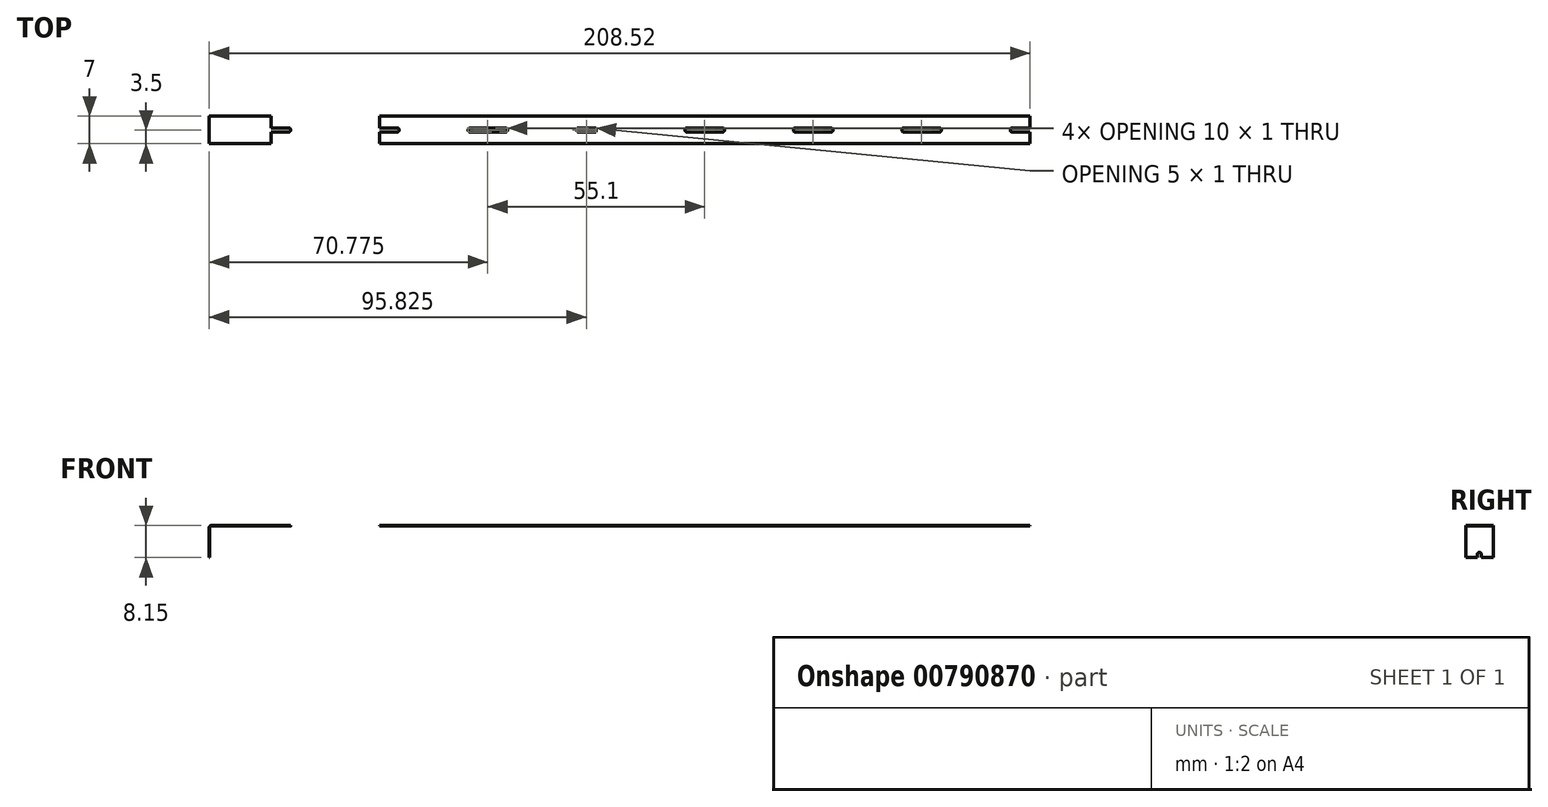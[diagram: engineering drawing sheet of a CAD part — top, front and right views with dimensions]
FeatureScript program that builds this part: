
annotation { "Feature Type Name" : "Feature", "Feature Type Description" : "" }
export const myFeature = defineFeature(function(context is Context, id is Id, definition is map)
    precondition{}
    {
        {
            var Q0;
            Q0=qCreatedBy(makeId("Top.planeOp"),FACE);
            var sketch = newSketch(context, id + "F0", { "sketchPlane" : qUnion([Q0])});
            skPoint(sketch, "E0.middle", {"position": v(0, 0) * mm});
            skLineSegment(sketch, "E1.bottom", {"start": v(-9.18, -0.5) * mm, "end": v(-13.77, -0.5) * mm});
            skLineSegment(sketch, "E1.top", {"start": v(-9.18, 0.5) * mm, "end": v(-13.77, 0.5) * mm});
            skLineSegment(sketch, "E1.left", {"start": v(-8.78, -0.1) * mm, "end": v(-8.78, 0.1) * mm});
            skLineSegment(sketch, "E1.right", {"start": v(-18.78, -0.1) * mm, "end": v(-18.78, 0.1) * mm});
            skPoint(sketch, "E1.middle", {"position": v(-13.78, 0) * mm});
            skPoint(sketch, "E2.visualSharp", {"position": v(-8.78, 0.5) * mm});
            skArc(sketch, "E2.filletArc", {"start": v(-8.78, 0.1) * mm, "mid": v(-8.9, 0.38) * mm, "end": v(-9.18, 0.5) * mm});
            skPoint(sketch, "E3.visualSharp", {"position": v(-8.78, -0.5) * mm});
            skArc(sketch, "E3.filletArc", {"start": v(-9.18, -0.5) * mm, "mid": v(-8.9, -0.38) * mm, "end": v(-8.78, -0.1) * mm});
            skPoint(sketch, "E4.visualSharp", {"position": v(-18.78, 0.5) * mm});
            skArc(sketch, "E4.filletArc", {"start": v(-18.38, 0.5) * mm, "mid": v(-18.66, 0.38) * mm, "end": v(-18.77, 0.1) * mm});
            skPoint(sketch, "E5.visualSharp", {"position": v(-18.78, -0.5) * mm});
            skArc(sketch, "E5.filletArc", {"start": v(-18.77, -0.1) * mm, "mid": v(-18.66, -0.38) * mm, "end": v(-18.38, -0.5) * mm});
            skLineSegment(sketch, "E6", {"start": v(0, 3.5) * mm, "end": v(-13.78, 3.5) * mm});
            skPoint(sketch, "E6.endSnap0", {"position": v(-13.77, 0.5) * mm});
            skLineSegment(sketch, "E7", {"start": v(-13.78, 3.5) * mm, "end": v(-13.78, 0.5) * mm});
            skLineSegment(sketch, "E8.MirrorCS", {"start": v(0, -3.5) * mm, "end": v(-13.78, -3.5) * mm});
            skLineSegment(sketch, "E9.MirrorCS", {"start": v(-13.78, -3.5) * mm, "end": v(-13.78, -0.5) * mm});
            skLineSegment(sketch, "E10.MirrorCS", {"start": v(0, 3.5) * mm, "end": v(13.78, 3.5) * mm});
            skLineSegment(sketch, "E11.MirrorCS", {"start": v(0, -3.5) * mm, "end": v(13.78, -3.5) * mm});
            skLineSegment(sketch, "E12.MirrorCS", {"start": v(8.78, -0.1) * mm, "end": v(8.78, 0.1) * mm});
            skArc(sketch, "E13.MirrorCS", {"start": v(8.78, 0.1) * mm, "mid": v(8.9, 0.38) * mm, "end": v(9.18, 0.5) * mm});
            skArc(sketch, "E14.MirrorCS", {"start": v(18.77, -0.1) * mm, "mid": v(18.66, -0.38) * mm, "end": v(18.38, -0.5) * mm});
            skLineSegment(sketch, "E15.MirrorCS", {"start": v(18.78, -0.1) * mm, "end": v(18.78, 0.1) * mm});
            skArc(sketch, "E16.MirrorCS", {"start": v(18.38, 0.5) * mm, "mid": v(18.66, 0.38) * mm, "end": v(18.77, 0.1) * mm});
            skArc(sketch, "E17.MirrorCS", {"start": v(9.18, -0.5) * mm, "mid": v(8.9, -0.38) * mm, "end": v(8.78, -0.1) * mm});
            skPoint(sketch, "E18.MirrorP", {"position": v(18.78, 0.5) * mm});
            skLineSegment(sketch, "E19.MirrorCS", {"start": v(9.18, 0.5) * mm, "end": v(18.38, 0.5) * mm});
            skLineSegment(sketch, "E20.MirrorCS", {"start": v(9.18, -0.5) * mm, "end": v(18.38, -0.5) * mm});
            skPoint(sketch, "E21.MirrorP", {"position": v(13.77, 0.5) * mm});
            skPoint(sketch, "E22.MirrorP", {"position": v(8.78, 0.5) * mm});
            skPoint(sketch, "E23.MirrorP", {"position": v(18.78, -0.5) * mm});
            skPoint(sketch, "E24.MirrorP", {"position": v(8.78, -0.5) * mm});
            skPoint(sketch, "E25.MirrorP", {"position": v(13.78, 0) * mm});
            skLineSegment(sketch, "E26.MirrorCS", {"start": v(13.78, 3.5) * mm, "end": v(13.78, 0.5) * mm});
            skLineSegment(sketch, "E27.MirrorCS", {"start": v(13.78, -3.5) * mm, "end": v(13.78, -0.5) * mm});
            skPoint(sketch, "E28.1.0.0", {"position": v(36.33, 0.5) * mm});
            skLineSegment(sketch, "E28.1.0.1", {"start": v(27.55, 3.5) * mm, "end": v(41.33, 3.5) * mm});
            skLineSegment(sketch, "E28.1.0.2", {"start": v(36.73, -0.5) * mm, "end": v(45.93, -0.5) * mm});
            skPoint(sketch, "E28.1.0.3", {"position": v(27.55, 0) * mm});
            skLineSegment(sketch, "E28.1.0.4", {"start": v(27.55, -3.5) * mm, "end": v(41.33, -3.5) * mm});
            skPoint(sketch, "E28.1.0.5", {"position": v(41.33, 0.5) * mm});
            skPoint(sketch, "E28.1.0.6", {"position": v(41.33, 0) * mm});
            skPoint(sketch, "E28.1.0.7", {"position": v(46.33, -0.5) * mm});
            skPoint(sketch, "E28.1.0.8", {"position": v(36.33, -0.5) * mm});
            skLineSegment(sketch, "E28.1.0.9", {"start": v(27.55, -3.5) * mm, "end": v(13.78, -3.5) * mm});
            skLineSegment(sketch, "E28.1.0.10", {"start": v(36.73, 0.5) * mm, "end": v(45.93, 0.5) * mm});
            skLineSegment(sketch, "E28.1.0.11", {"start": v(27.55, 3.5) * mm, "end": v(13.78, 3.5) * mm});
            skLineSegment(sketch, "E28.1.0.12", {"start": v(41.33, 3.5) * mm, "end": v(41.33, 0.5) * mm});
            skLineSegment(sketch, "E28.1.0.13", {"start": v(41.33, -3.5) * mm, "end": v(41.33, -0.5) * mm});
            skPoint(sketch, "E28.1.0.14", {"position": v(46.33, 0.5) * mm});
            skArc(sketch, "E28.1.0.15", {"start": v(45.93, 0.5) * mm, "mid": v(46.2, 0.38) * mm, "end": v(46.32, 0.1) * mm});
            skArc(sketch, "E28.1.0.16", {"start": v(36.73, -0.5) * mm, "mid": v(36.44, -0.38) * mm, "end": v(36.33, -0.1) * mm});
            skArc(sketch, "E28.1.0.17", {"start": v(46.33, -0.1) * mm, "mid": v(46.2, -0.38) * mm, "end": v(45.93, -0.5) * mm});
            skArc(sketch, "E28.1.0.18", {"start": v(36.33, 0.1) * mm, "mid": v(36.44, 0.38) * mm, "end": v(36.73, 0.5) * mm});
            skLineSegment(sketch, "E28.1.0.19", {"start": v(36.32, -0.1) * mm, "end": v(36.32, 0.1) * mm});
            skLineSegment(sketch, "E28.1.0.20", {"start": v(46.33, -0.1) * mm, "end": v(46.33, 0.1) * mm});
            skPoint(sketch, "E28.2.0.0", {"position": v(63.88, 0.5) * mm});
            skLineSegment(sketch, "E28.2.0.1", {"start": v(55.1, 3.5) * mm, "end": v(68.88, 3.5) * mm});
            skLineSegment(sketch, "E28.2.0.2", {"start": v(64.28, -0.5) * mm, "end": v(73.48, -0.5) * mm});
            skPoint(sketch, "E28.2.0.3", {"position": v(55.1, 0) * mm});
            skLineSegment(sketch, "E28.2.0.4", {"start": v(55.1, -3.5) * mm, "end": v(68.88, -3.5) * mm});
            skPoint(sketch, "E28.2.0.5", {"position": v(68.88, 0.5) * mm});
            skPoint(sketch, "E28.2.0.6", {"position": v(68.88, 0) * mm});
            skPoint(sketch, "E28.2.0.7", {"position": v(73.88, -0.5) * mm});
            skPoint(sketch, "E28.2.0.8", {"position": v(63.88, -0.5) * mm});
            skLineSegment(sketch, "E28.2.0.9", {"start": v(55.1, -3.5) * mm, "end": v(41.33, -3.5) * mm});
            skLineSegment(sketch, "E28.2.0.10", {"start": v(64.28, 0.5) * mm, "end": v(73.48, 0.5) * mm});
            skLineSegment(sketch, "E28.2.0.11", {"start": v(55.1, 3.5) * mm, "end": v(41.33, 3.5) * mm});
            skLineSegment(sketch, "E28.2.0.12", {"start": v(68.88, 3.5) * mm, "end": v(68.88, 0.5) * mm});
            skLineSegment(sketch, "E28.2.0.13", {"start": v(68.88, -3.5) * mm, "end": v(68.88, -0.5) * mm});
            skPoint(sketch, "E28.2.0.14", {"position": v(73.88, 0.5) * mm});
            skArc(sketch, "E28.2.0.15", {"start": v(73.48, 0.5) * mm, "mid": v(73.76, 0.38) * mm, "end": v(73.88, 0.1) * mm});
            skArc(sketch, "E28.2.0.16", {"start": v(64.28, -0.5) * mm, "mid": v(64, -0.38) * mm, "end": v(63.88, -0.1) * mm});
            skArc(sketch, "E28.2.0.17", {"start": v(73.88, -0.1) * mm, "mid": v(73.76, -0.38) * mm, "end": v(73.48, -0.5) * mm});
            skArc(sketch, "E28.2.0.18", {"start": v(63.88, 0.1) * mm, "mid": v(64, 0.38) * mm, "end": v(64.28, 0.5) * mm});
            skLineSegment(sketch, "E28.2.0.19", {"start": v(63.88, -0.1) * mm, "end": v(63.88, 0.1) * mm});
            skLineSegment(sketch, "E28.2.0.20", {"start": v(73.88, -0.1) * mm, "end": v(73.88, 0.1) * mm});
            skPoint(sketch, "E28.3.0.0", {"position": v(91.43, 0.5) * mm});
            skLineSegment(sketch, "E28.3.0.1", {"start": v(82.65, 3.5) * mm, "end": v(96.43, 3.5) * mm});
            skLineSegment(sketch, "E28.3.0.2", {"start": v(91.83, -0.5) * mm, "end": v(101.03, -0.5) * mm});
            skPoint(sketch, "E28.3.0.3", {"position": v(82.65, 0) * mm});
            skLineSegment(sketch, "E28.3.0.4", {"start": v(82.65, -3.5) * mm, "end": v(96.43, -3.5) * mm});
            skPoint(sketch, "E28.3.0.5", {"position": v(96.43, 0.5) * mm});
            skPoint(sketch, "E28.3.0.6", {"position": v(96.42, 0) * mm});
            skPoint(sketch, "E28.3.0.7", {"position": v(101.42, -0.5) * mm});
            skPoint(sketch, "E28.3.0.8", {"position": v(91.43, -0.5) * mm});
            skLineSegment(sketch, "E28.3.0.9", {"start": v(82.65, -3.5) * mm, "end": v(68.88, -3.5) * mm});
            skLineSegment(sketch, "E28.3.0.10", {"start": v(91.83, 0.5) * mm, "end": v(101.03, 0.5) * mm});
            skLineSegment(sketch, "E28.3.0.11", {"start": v(82.65, 3.5) * mm, "end": v(68.88, 3.5) * mm});
            skLineSegment(sketch, "E28.3.0.12", {"start": v(96.43, 3.5) * mm, "end": v(96.43, 0.5) * mm});
            skLineSegment(sketch, "E28.3.0.13", {"start": v(96.43, -3.5) * mm, "end": v(96.43, -0.5) * mm});
            skPoint(sketch, "E28.3.0.14", {"position": v(101.42, 0.5) * mm});
            skArc(sketch, "E28.3.0.15", {"start": v(101.03, 0.5) * mm, "mid": v(101.3, 0.38) * mm, "end": v(101.42, 0.1) * mm});
            skArc(sketch, "E28.3.0.16", {"start": v(91.83, -0.5) * mm, "mid": v(91.54, -0.38) * mm, "end": v(91.43, -0.1) * mm});
            skArc(sketch, "E28.3.0.17", {"start": v(101.42, -0.1) * mm, "mid": v(101.3, -0.38) * mm, "end": v(101.03, -0.5) * mm});
            skArc(sketch, "E28.3.0.18", {"start": v(91.43, 0.1) * mm, "mid": v(91.54, 0.38) * mm, "end": v(91.83, 0.5) * mm});
            skLineSegment(sketch, "E28.3.0.19", {"start": v(91.43, -0.1) * mm, "end": v(91.43, 0.1) * mm});
            skLineSegment(sketch, "E28.3.0.20", {"start": v(101.42, -0.1) * mm, "end": v(101.42, 0.1) * mm});
            skLineSegment(sketch, "E28.direction1", {"start": v(-13.78, -3.5) * mm, "end": v(13.78, -3.5) * mm, "construction": true});
            skLineSegment(sketch, "E29", {"start": v(0, 3.5) * mm, "end": v(0, -3.5) * mm});
            skLineSegment(sketch, "E30.bottom", {"start": v(96.43, -3.5) * mm, "end": v(99.43, -3.5) * mm});
            skLineSegment(sketch, "E30.top", {"start": v(96.43, 3.5) * mm, "end": v(99.43, 3.5) * mm});
            skLineSegment(sketch, "E30.left", {"start": v(96.43, -3.5) * mm, "end": v(96.43, 3.5) * mm});
            skPoint(sketch, "E31.0.4.0", {"position": v(118.98, 0.5) * mm});
            skLineSegment(sketch, "E31.1.4.0", {"start": v(110.2, 3.5) * mm, "end": v(123.98, 3.5) * mm});
            skLineSegment(sketch, "E31.4.4.0", {"start": v(119.38, -0.5) * mm, "end": v(128.57, -0.5) * mm});
            skPoint(sketch, "E31.7.4.0", {"position": v(110.2, 0) * mm});
            skLineSegment(sketch, "E31.8.4.0", {"start": v(110.2, -3.5) * mm, "end": v(123.98, -3.5) * mm});
            skPoint(sketch, "E31.11.4.0", {"position": v(123.98, 0.5) * mm});
            skPoint(sketch, "E31.12.4.0", {"position": v(123.98, 0) * mm});
            skPoint(sketch, "E31.13.4.0", {"position": v(128.97, -0.5) * mm});
            skPoint(sketch, "E31.14.4.0", {"position": v(118.98, -0.5) * mm});
            skLineSegment(sketch, "E31.15.4.0", {"start": v(110.2, -3.5) * mm, "end": v(96.43, -3.5) * mm});
            skLineSegment(sketch, "E31.18.4.0", {"start": v(119.38, 0.5) * mm, "end": v(128.57, 0.5) * mm});
            skLineSegment(sketch, "E31.21.4.0", {"start": v(110.2, 3.5) * mm, "end": v(96.43, 3.5) * mm});
            skLineSegment(sketch, "E31.24.4.0", {"start": v(123.98, 3.5) * mm, "end": v(123.98, 0.5) * mm});
            skLineSegment(sketch, "E31.27.4.0", {"start": v(123.98, -3.5) * mm, "end": v(123.98, -0.5) * mm});
            skPoint(sketch, "E31.30.4.0", {"position": v(128.97, 0.5) * mm});
            skArc(sketch, "E31.31.4.0", {"start": v(128.57, 0.5) * mm, "mid": v(128.86, 0.38) * mm, "end": v(128.97, 0.1) * mm});
            skArc(sketch, "E31.35.4.0", {"start": v(119.38, -0.5) * mm, "mid": v(119.1, -0.38) * mm, "end": v(118.98, -0.1) * mm});
            skArc(sketch, "E31.39.4.0", {"start": v(128.97, -0.1) * mm, "mid": v(128.86, -0.38) * mm, "end": v(128.57, -0.5) * mm});
            skArc(sketch, "E31.43.4.0", {"start": v(118.98, 0.1) * mm, "mid": v(119.1, 0.38) * mm, "end": v(119.38, 0.5) * mm});
            skLineSegment(sketch, "E31.47.4.0", {"start": v(118.98, -0.1) * mm, "end": v(118.98, 0.1) * mm});
            skLineSegment(sketch, "E31.50.4.0", {"start": v(128.97, -0.1) * mm, "end": v(128.97, 0.1) * mm});
            skPoint(sketch, "E31.0.5.0", {"position": v(146.53, 0.5) * mm});
            skLineSegment(sketch, "E31.1.5.0", {"start": v(137.75, 3.5) * mm, "end": v(151.53, 3.5) * mm});
            skLineSegment(sketch, "E31.4.5.0", {"start": v(146.93, -0.5) * mm, "end": v(156.12, -0.5) * mm});
            skPoint(sketch, "E31.7.5.0", {"position": v(137.75, 0) * mm});
            skLineSegment(sketch, "E31.8.5.0", {"start": v(137.75, -3.5) * mm, "end": v(151.53, -3.5) * mm});
            skPoint(sketch, "E31.11.5.0", {"position": v(151.53, 0.5) * mm});
            skPoint(sketch, "E31.12.5.0", {"position": v(151.53, 0) * mm});
            skPoint(sketch, "E31.13.5.0", {"position": v(156.53, -0.5) * mm});
            skPoint(sketch, "E31.14.5.0", {"position": v(146.53, -0.5) * mm});
            skLineSegment(sketch, "E31.15.5.0", {"start": v(137.75, -3.5) * mm, "end": v(123.98, -3.5) * mm});
            skLineSegment(sketch, "E31.18.5.0", {"start": v(146.93, 0.5) * mm, "end": v(156.12, 0.5) * mm});
            skLineSegment(sketch, "E31.21.5.0", {"start": v(137.75, 3.5) * mm, "end": v(123.98, 3.5) * mm});
            skLineSegment(sketch, "E31.24.5.0", {"start": v(151.53, 3.5) * mm, "end": v(151.53, 0.5) * mm});
            skLineSegment(sketch, "E31.27.5.0", {"start": v(151.53, -3.5) * mm, "end": v(151.53, -0.5) * mm});
            skPoint(sketch, "E31.30.5.0", {"position": v(156.53, 0.5) * mm});
            skArc(sketch, "E31.31.5.0", {"start": v(156.12, 0.5) * mm, "mid": v(156.4, 0.38) * mm, "end": v(156.53, 0.1) * mm});
            skArc(sketch, "E31.35.5.0", {"start": v(146.93, -0.5) * mm, "mid": v(146.64, -0.38) * mm, "end": v(146.52, -0.1) * mm});
            skArc(sketch, "E31.39.5.0", {"start": v(156.53, -0.1) * mm, "mid": v(156.4, -0.38) * mm, "end": v(156.12, -0.5) * mm});
            skArc(sketch, "E31.43.5.0", {"start": v(146.53, 0.1) * mm, "mid": v(146.64, 0.38) * mm, "end": v(146.93, 0.5) * mm});
            skLineSegment(sketch, "E31.47.5.0", {"start": v(146.53, -0.1) * mm, "end": v(146.53, 0.1) * mm});
            skLineSegment(sketch, "E31.50.5.0", {"start": v(156.53, -0.1) * mm, "end": v(156.53, 0.1) * mm});
            skPoint(sketch, "E31.0.6.0", {"position": v(174.08, 0.5) * mm});
            skLineSegment(sketch, "E31.1.6.0", {"start": v(165.3, 3.5) * mm, "end": v(179.08, 3.5) * mm});
            skLineSegment(sketch, "E31.4.6.0", {"start": v(174.47, -0.5) * mm, "end": v(183.68, -0.5) * mm});
            skPoint(sketch, "E31.7.6.0", {"position": v(165.3, 0) * mm});
            skLineSegment(sketch, "E31.8.6.0", {"start": v(165.3, -3.5) * mm, "end": v(179.08, -3.5) * mm});
            skPoint(sketch, "E31.11.6.0", {"position": v(179.07, 0.5) * mm});
            skPoint(sketch, "E31.12.6.0", {"position": v(179.08, 0) * mm});
            skPoint(sketch, "E31.13.6.0", {"position": v(184.08, -0.5) * mm});
            skPoint(sketch, "E31.14.6.0", {"position": v(174.08, -0.5) * mm});
            skLineSegment(sketch, "E31.15.6.0", {"start": v(165.3, -3.5) * mm, "end": v(151.53, -3.5) * mm});
            skLineSegment(sketch, "E31.18.6.0", {"start": v(174.47, 0.5) * mm, "end": v(183.68, 0.5) * mm});
            skLineSegment(sketch, "E31.21.6.0", {"start": v(165.3, 3.5) * mm, "end": v(151.53, 3.5) * mm});
            skLineSegment(sketch, "E31.24.6.0", {"start": v(179.08, 3.5) * mm, "end": v(179.08, 0.5) * mm});
            skLineSegment(sketch, "E31.27.6.0", {"start": v(179.08, -3.5) * mm, "end": v(179.08, -0.5) * mm});
            skPoint(sketch, "E31.30.6.0", {"position": v(184.08, 0.5) * mm});
            skArc(sketch, "E31.31.6.0", {"start": v(183.68, 0.5) * mm, "mid": v(183.96, 0.38) * mm, "end": v(184.08, 0.1) * mm});
            skArc(sketch, "E31.35.6.0", {"start": v(174.47, -0.5) * mm, "mid": v(174.2, -0.38) * mm, "end": v(174.07, -0.1) * mm});
            skArc(sketch, "E31.39.6.0", {"start": v(184.07, -0.1) * mm, "mid": v(183.96, -0.38) * mm, "end": v(183.68, -0.5) * mm});
            skArc(sketch, "E31.43.6.0", {"start": v(174.07, 0.1) * mm, "mid": v(174.2, 0.38) * mm, "end": v(174.47, 0.5) * mm});
            skLineSegment(sketch, "E31.47.6.0", {"start": v(174.08, -0.1) * mm, "end": v(174.08, 0.1) * mm});
            skLineSegment(sketch, "E31.50.6.0", {"start": v(184.08, -0.1) * mm, "end": v(184.08, 0.1) * mm});
            skPoint(sketch, "E31.0.7.0", {"position": v(201.63, 0.5) * mm});
            skLineSegment(sketch, "E31.1.7.0", {"start": v(192.85, 3.5) * mm, "end": v(206.63, 3.5) * mm});
            skLineSegment(sketch, "E31.4.7.0", {"start": v(202.03, -0.5) * mm, "end": v(211.23, -0.5) * mm});
            skPoint(sketch, "E31.7.7.0", {"position": v(192.85, 0) * mm});
            skLineSegment(sketch, "E31.8.7.0", {"start": v(192.85, -3.5) * mm, "end": v(206.63, -3.5) * mm});
            skPoint(sketch, "E31.11.7.0", {"position": v(206.62, 0.5) * mm});
            skPoint(sketch, "E31.12.7.0", {"position": v(206.63, 0) * mm});
            skPoint(sketch, "E31.13.7.0", {"position": v(211.63, -0.5) * mm});
            skPoint(sketch, "E31.14.7.0", {"position": v(201.63, -0.5) * mm});
            skLineSegment(sketch, "E31.15.7.0", {"start": v(192.85, -3.5) * mm, "end": v(179.08, -3.5) * mm});
            skLineSegment(sketch, "E31.18.7.0", {"start": v(202.03, 0.5) * mm, "end": v(211.23, 0.5) * mm});
            skLineSegment(sketch, "E31.21.7.0", {"start": v(192.85, 3.5) * mm, "end": v(179.08, 3.5) * mm});
            skLineSegment(sketch, "E31.24.7.0", {"start": v(206.63, 3.5) * mm, "end": v(206.63, 0.5) * mm});
            skLineSegment(sketch, "E31.27.7.0", {"start": v(206.63, -3.5) * mm, "end": v(206.63, -0.5) * mm});
            skPoint(sketch, "E31.30.7.0", {"position": v(211.63, 0.5) * mm});
            skArc(sketch, "E31.31.7.0", {"start": v(211.23, 0.5) * mm, "mid": v(211.5, 0.38) * mm, "end": v(211.63, 0.1) * mm});
            skArc(sketch, "E31.35.7.0", {"start": v(202.03, -0.5) * mm, "mid": v(201.74, -0.38) * mm, "end": v(201.62, -0.1) * mm});
            skArc(sketch, "E31.39.7.0", {"start": v(211.62, -0.1) * mm, "mid": v(211.5, -0.38) * mm, "end": v(211.23, -0.5) * mm});
            skArc(sketch, "E31.43.7.0", {"start": v(201.62, 0.1) * mm, "mid": v(201.74, 0.38) * mm, "end": v(202.03, 0.5) * mm});
            skLineSegment(sketch, "E31.47.7.0", {"start": v(201.63, -0.1) * mm, "end": v(201.63, 0.1) * mm});
            skLineSegment(sketch, "E31.50.7.0", {"start": v(211.63, -0.1) * mm, "end": v(211.63, 0.1) * mm});
            skSolve(sketch);
        }
        {
            var Q0;
            {var subQ8=sQuery(id+"F0.wireOp",EDGE,"E28.3.0.12");Q0=makeQuery(id+"F0.imprint","IMPRINT",FACE,{"disambiguationData":[TD([[makeQuery(id+"F0.imprint","IMPRINT",EDGE,{"derivedFrom":subQ8}),1.0]])]});}
            var Q1;
            {var subQ3=sQuery(id+"F0.wireOp",EDGE,"E14.MirrorCS");Q1=makeQuery(id+"F0.imprint","IMPRINT",FACE,{"disambiguationData":[TD([[makeQuery(id+"F0.imprint","IMPRINT",EDGE,{"derivedFrom":subQ3}),1.0]])]});}
            var Q2;
            {var subQ8=sQuery(id+"F0.wireOp",EDGE,"E28.1.0.12");Q2=makeQuery(id+"F0.imprint","IMPRINT",FACE,{"disambiguationData":[TD([[makeQuery(id+"F0.imprint","IMPRINT",EDGE,{"derivedFrom":subQ8}),1.0]])]});}
            var Q3;
            {var subQ8=sQuery(id+"F0.wireOp",EDGE,"E28.2.0.12");Q3=makeQuery(id+"F0.imprint","IMPRINT",FACE,{"disambiguationData":[TD([[makeQuery(id+"F0.imprint","IMPRINT",EDGE,{"derivedFrom":subQ8}),1.0]])]});}
            var Q4;
            Q4=makeQuery(id+"F0.imprint","IMPRINT",FACE,{"disambiguationData":[TD([[makeQuery(id+"F0.imprint","IMPRINT",EDGE,{"derivedFrom":sQuery(id+"F0.wireOp",EDGE,"E10.MirrorCS")}),-1.0]])]});
            var Q5;
            {var subQ5=sQuery(id+"F0.wireOp",EDGE,"E30.top");Q5=makeQuery(id+"F0.imprint","IMPRINT",FACE,{"disambiguationData":[TD([[makeQuery(id+"F0.imprint","IMPRINT",EDGE,{"derivedFrom":subQ5}),-1.0]])]});}
            var Q6;
            {var subQ5=sQuery(id+"F0.wireOp",EDGE,"E30.bottom");Q6=makeQuery(id+"F0.imprint","IMPRINT",FACE,{"disambiguationData":[TD([[makeQuery(id+"F0.imprint","IMPRINT",EDGE,{"derivedFrom":subQ5}),1.0]])]});}
            var Q7;
            {var subQ11=sQuery(id+"F0.wireOp",EDGE,"E28.3.0.15");Q7=makeQuery(id+"F0.imprint","IMPRINT",FACE,{"disambiguationData":[TD([[makeQuery(id+"F0.imprint","IMPRINT",EDGE,{"derivedFrom":subQ11}),1.0]])]});}
            var Q8;
            {var subQ8=sQuery(id+"F0.wireOp",EDGE,"E31.24.4.0");Q8=makeQuery(id+"F0.imprint","IMPRINT",FACE,{"disambiguationData":[TD([[makeQuery(id+"F0.imprint","IMPRINT",EDGE,{"derivedFrom":subQ8}),1.0]])]});}
            var Q9;
            {var subQ8=sQuery(id+"F0.wireOp",EDGE,"E31.24.5.0");Q9=makeQuery(id+"F0.imprint","IMPRINT",FACE,{"disambiguationData":[TD([[makeQuery(id+"F0.imprint","IMPRINT",EDGE,{"derivedFrom":subQ8}),1.0]])]});}
            var Q10;
            {var subQ8=sQuery(id+"F0.wireOp",EDGE,"E31.24.6.0");Q10=makeQuery(id+"F0.imprint","IMPRINT",FACE,{"disambiguationData":[TD([[makeQuery(id+"F0.imprint","IMPRINT",EDGE,{"derivedFrom":subQ8}),1.0]])]});}
            extrude(context, id + "F1", {"entities" : qUnion([Q0, Q1, Q2, Q3, Q4, Q5, Q6, Q7, Q8, Q9, Q10]), "depth" : 0.15 * mm, "offsetDistance" : 25 * mm});
        }
        {
            var Q0;
            Q0=makeQuery(id+"F1.opExtrude","SWEPT_FACE",FACE,{"disambiguationData":[OSD([sQuery(id+"F0.wireOp",EDGE,"E29")])]});
            extrude(context, id + "F2", {"entities" : qUnion([Q0]), "operationType" : NewBodyOperationType.ADD, "depth" : 1.9 * mm, "offsetDistance" : 25 * mm});
        }
        {
            var Q0;
            {var subQ0=sQuery(id+"F0.wireOp",EDGE,"E29");Q0=makeQuery(id+"F2.boolean.opBoolean","MERGE",FACE,{"derivedFrom":[makeQuery(id+"F1.opExtrude","CAP_FACE",FACE,{"disambiguationData":[OSD([sQuery(id+"F0.wireOp",EDGE,"E10.MirrorCS"),sQuery(id+"F0.wireOp",EDGE,"E11.MirrorCS"),sQuery(id+"F0.wireOp",EDGE,"E12.MirrorCS"),sQuery(id+"F0.wireOp",EDGE,"E13.MirrorCS"),sQuery(id+"F0.wireOp",EDGE,"E14.MirrorCS"),sQuery(id+"F0.wireOp",EDGE,"E15.MirrorCS"),sQuery(id+"F0.wireOp",EDGE,"E16.MirrorCS"),sQuery(id+"F0.wireOp",EDGE,"E17.MirrorCS"),sQuery(id+"F0.wireOp",EDGE,"E19.MirrorCS"),sQuery(id+"F0.wireOp",EDGE,"E20.MirrorCS"),sQuery(id+"F0.wireOp",EDGE,"E28.1.0.1"),sQuery(id+"F0.wireOp",EDGE,"E28.1.0.2"),sQuery(id+"F0.wireOp",EDGE,"E28.1.0.4"),sQuery(id+"F0.wireOp",EDGE,"E28.1.0.9"),sQuery(id+"F0.wireOp",EDGE,"E28.1.0.10"),sQuery(id+"F0.wireOp",EDGE,"E28.1.0.11"),sQuery(id+"F0.wireOp",EDGE,"E28.1.0.15"),sQuery(id+"F0.wireOp",EDGE,"E28.1.0.16"),sQuery(id+"F0.wireOp",EDGE,"E28.1.0.17"),sQuery(id+"F0.wireOp",EDGE,"E28.1.0.18"),sQuery(id+"F0.wireOp",EDGE,"E28.1.0.19"),sQuery(id+"F0.wireOp",EDGE,"E28.1.0.20"),sQuery(id+"F0.wireOp",EDGE,"E28.2.0.1"),sQuery(id+"F0.wireOp",EDGE,"E28.2.0.2"),sQuery(id+"F0.wireOp",EDGE,"E28.2.0.4"),sQuery(id+"F0.wireOp",EDGE,"E28.2.0.9"),sQuery(id+"F0.wireOp",EDGE,"E28.2.0.10"),sQuery(id+"F0.wireOp",EDGE,"E28.2.0.11"),sQuery(id+"F0.wireOp",EDGE,"E28.2.0.15"),sQuery(id+"F0.wireOp",EDGE,"E28.2.0.16"),sQuery(id+"F0.wireOp",EDGE,"E28.2.0.17"),sQuery(id+"F0.wireOp",EDGE,"E28.2.0.18"),sQuery(id+"F0.wireOp",EDGE,"E28.2.0.19"),sQuery(id+"F0.wireOp",EDGE,"E28.2.0.20"),sQuery(id+"F0.wireOp",EDGE,"E28.3.0.1"),sQuery(id+"F0.wireOp",EDGE,"E28.3.0.2"),sQuery(id+"F0.wireOp",EDGE,"E28.3.0.4"),sQuery(id+"F0.wireOp",EDGE,"E28.3.0.9"),sQuery(id+"F0.wireOp",EDGE,"E28.3.0.10"),sQuery(id+"F0.wireOp",EDGE,"E28.3.0.11"),sQuery(id+"F0.wireOp",EDGE,"E28.3.0.12"),sQuery(id+"F0.wireOp",EDGE,"E28.3.0.13"),sQuery(id+"F0.wireOp",EDGE,"E28.3.0.16"),sQuery(id+"F0.wireOp",EDGE,"E28.3.0.18"),sQuery(id+"F0.wireOp",EDGE,"E28.3.0.19"),subQ0])],"isStart":true}),makeQuery(id+"F2.opExtrude","SWEPT_FACE",FACE,{"disambiguationData":[OSD([subQ0]),TDD([makeQuery(id+"F1.opExtrude","CAP_EDGE",EDGE,{"disambiguationData":[OSD([subQ0])],"isStart":true})])]})]});}
            var sketch = newSketch(context, id + "F3", { "sketchPlane" : qUnion([Q0])});
            skLineSegment(sketch, "E32.bottom", {"start": v(-1.9, -3.5) * mm, "end": v(-1.75, -3.5) * mm});
            skLineSegment(sketch, "E32.top", {"start": v(-1.9, 3.5) * mm, "end": v(-1.75, 3.5) * mm});
            skLineSegment(sketch, "E32.left", {"start": v(-1.9, -3.5) * mm, "end": v(-1.9, 3.5) * mm});
            skLineSegment(sketch, "E32.right", {"start": v(-1.75, -3.5) * mm, "end": v(-1.75, 3.5) * mm});
            skSolve(sketch);
        }
        {
            var Q0;
            Q0=qSketchRegion(id+"F3",true);
            extrude(context, id + "F4", {"entities" : qUnion([Q0]), "operationType" : NewBodyOperationType.ADD, "depth" : 8 * mm, "offsetDistance" : 25 * mm});
        }
        {
            var Q0;
            Q0=makeQuery(id+"F4.boolean.opBoolean","MERGE",FACE,{"derivedFrom":[makeQuery(id+"F2.opExtrude","CAP_FACE",FACE,{"disambiguationData":[OSD([sQuery(id+"F0.wireOp",EDGE,"E29")])],"isStart":false}),makeQuery(id+"F4.opExtrude","SWEPT_FACE",FACE,{"disambiguationData":[OSD([sQuery(id+"F3.wireOp",EDGE,"E32.left")])]})]});
            var sketch = newSketch(context, id + "F5", { "sketchPlane" : qUnion([Q0])});
            skLineSegment(sketch, "E33.bottom", {"start": v(0.1, -6.7) * mm, "end": v(-0.1, -6.7) * mm});
            skLineSegment(sketch, "E33.top", {"start": v(0.5, -16.7) * mm, "end": v(-0.5, -16.7) * mm});
            skLineSegment(sketch, "E33.left", {"start": v(0.5, -7.1) * mm, "end": v(0.5, -16.7) * mm});
            skLineSegment(sketch, "E33.right", {"start": v(-0.5, -7.1) * mm, "end": v(-0.5, -16.7) * mm});
            skPoint(sketch, "E33.middle", {"position": v(0, -11.7) * mm});
            skPoint(sketch, "E33.middle.positionSnap0", {"position": v(0, -8) * mm});
            skPoint(sketch, "E33.centerSnap0", {"position": v(0, -8) * mm});
            skPoint(sketch, "E34.visualSharp", {"position": v(-0.5, -6.7) * mm});
            skArc(sketch, "E34.filletArc", {"start": v(-0.1, -6.7) * mm, "mid": v(-0.38, -6.82) * mm, "end": v(-0.5, -7.1) * mm});
            skPoint(sketch, "E35.visualSharp", {"position": v(0.5, -6.7) * mm});
            skArc(sketch, "E35.filletArc", {"start": v(0.5, -7.1) * mm, "mid": v(0.38, -6.82) * mm, "end": v(0.1, -6.7) * mm});
            skSolve(sketch);
        }
        {
            var Q0;
            Q0=makeQuery(id+"F5.imprint","IMPRINT",FACE,{"disambiguationData":[TD([[makeQuery(id+"F5.imprint","IMPRINT",EDGE,{"derivedFrom":sQuery(id+"F5.wireOp",EDGE,"E33.bottom")}),1.0]])]});
            extrude(context, id + "F6", {"entities" : qUnion([Q0]), "operationType" : NewBodyOperationType.REMOVE, "oppositeDirection" : true, "depth" : 25 * mm, "offsetDistance" : 25 * mm});
        }
        {
            var Q0;
            {var subQ0=sQuery(id+"F0.wireOp",EDGE,"E29");Q0=makeQuery(id+"F2.opExtrude","CAP_EDGE",EDGE,{"disambiguationData":[OSD([subQ0]),TDD([makeQuery(id+"F1.opExtrude","CAP_EDGE",EDGE,{"disambiguationData":[OSD([subQ0])],"isStart":false})])],"isStart":false});}
            var Q1;
            Q1=makeQuery(id+"F4.opExtrude","CAP_EDGE",EDGE,{"disambiguationData":[OSD([sQuery(id+"F3.wireOp",EDGE,"E32.right")])],"isStart":true});
            fillet(context, id + "F7", {"entities" : qUnion([Q0, Q1]), "radius" : 0.5 * mm, "tangentPropagation" : true, "allowEdgeOverflow" : false});
        }
    });
